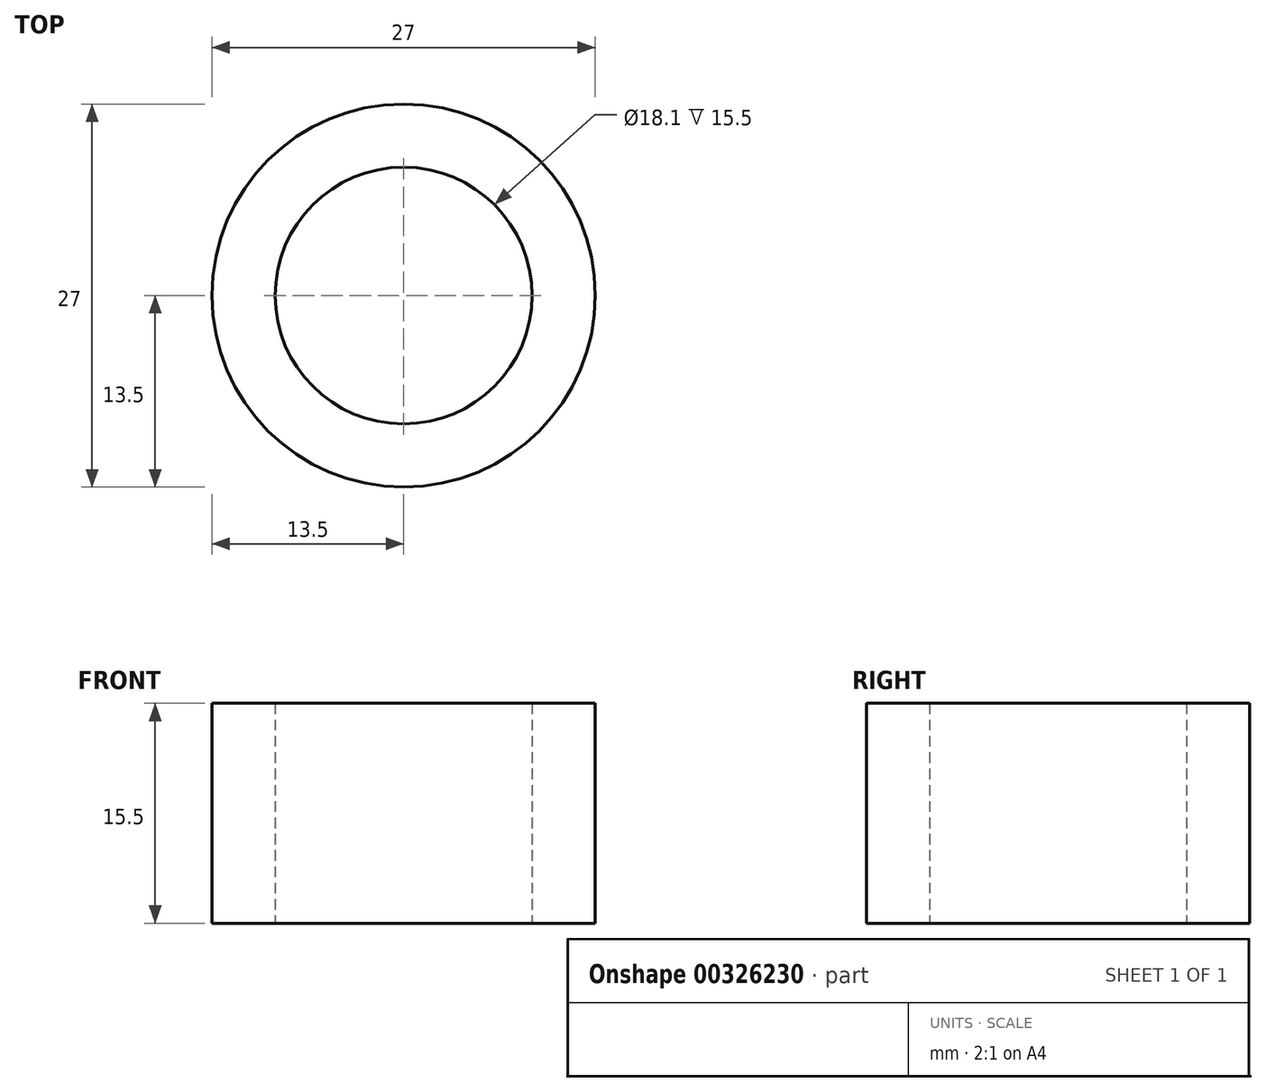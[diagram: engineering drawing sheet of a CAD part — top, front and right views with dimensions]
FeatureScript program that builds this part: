
annotation { "Feature Type Name" : "Feature", "Feature Type Description" : "" }
export const myFeature = defineFeature(function(context is Context, id is Id, definition is map)
    precondition{}
    {
        {
            var Q0;
            Q0=qCreatedBy(makeId("Top.planeOp"),FACE);
            var sketch = newSketch(context, id + "F0", { "sketchPlane" : qUnion([Q0])});
            skCircle(sketch, "E0", {"center": v(0, 0) * mm, "radius": 9.05 * mm});
            skCircle(sketch, "E1", {"center": v(0, 0) * mm, "radius": 13.5 * mm});
            skSolve(sketch);
        }
        {
            var Q0;
            Q0 = qSketchRegion(id + "F0", true);
            extrude(context, id + "F1", {"entities" : qUnion([Q0]), "depth" : 15.5 * mm});
        }
    });
